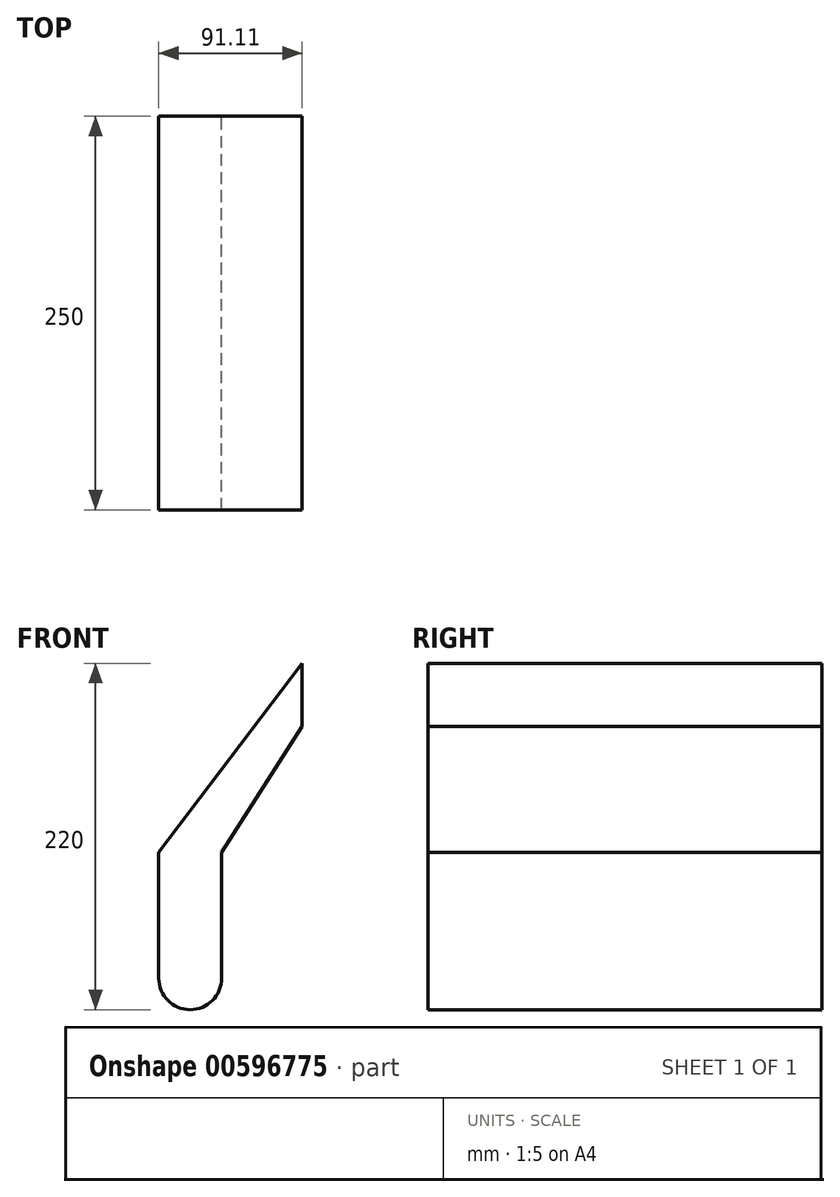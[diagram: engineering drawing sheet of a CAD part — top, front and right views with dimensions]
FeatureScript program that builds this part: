
annotation { "Feature Type Name" : "Feature", "Feature Type Description" : "" }
export const myFeature = defineFeature(function(context is Context, id is Id, definition is map)
    precondition{}
    {
        {
            var Q0;
            Q0=qCreatedBy(makeId("Front.planeOp"),FACE);
            var sketch = newSketch(context, id + "F0", { "sketchPlane" : qUnion([Q0])});
            skCircle(sketch, "E0", {"center": v(0, 0) * mm, "radius": 20 * mm});
            skPoint(sketch, "E1", {"position": v(-20, 0) * mm});
            skPoint(sketch, "E2", {"position": v(20, 0) * mm});
            skLineSegment(sketch, "E3", {"start": v(-20, 0) * mm, "end": v(-20, 80) * mm});
            skLineSegment(sketch, "E4", {"start": v(20, 0) * mm, "end": v(20, 80) * mm});
            skLineSegment(sketch, "E5", {"start": v(0, 0) * mm, "end": v(71.1, 0) * mm, "construction": true});
            skLineSegment(sketch, "E6", {"start": v(71.1, 0) * mm, "end": v(71.1, 200) * mm, "construction": true});
            skLineSegment(sketch, "E7", {"start": v(71.1, 200) * mm, "end": v(71.1, 160) * mm, "construction": true});
            skLineSegment(sketch, "E8", {"start": v(71.1, 160) * mm, "end": v(20, 80) * mm});
            skLineSegment(sketch, "E9", {"start": v(-20, 80) * mm, "end": v(71.1, 200) * mm});
            skLineSegment(sketch, "E10", {"start": v(71.1, 200) * mm, "end": v(71.1, 160) * mm});
            skSolve(sketch);
        }
        {
            var Q0;
            Q0 = qSketchRegion(id + "F0", true);
            extrude(context, id + "F1", {"entities" : qUnion([Q0]), "depth" : 250 * mm, "offsetDistance" : 25 * mm});
        }
    });
